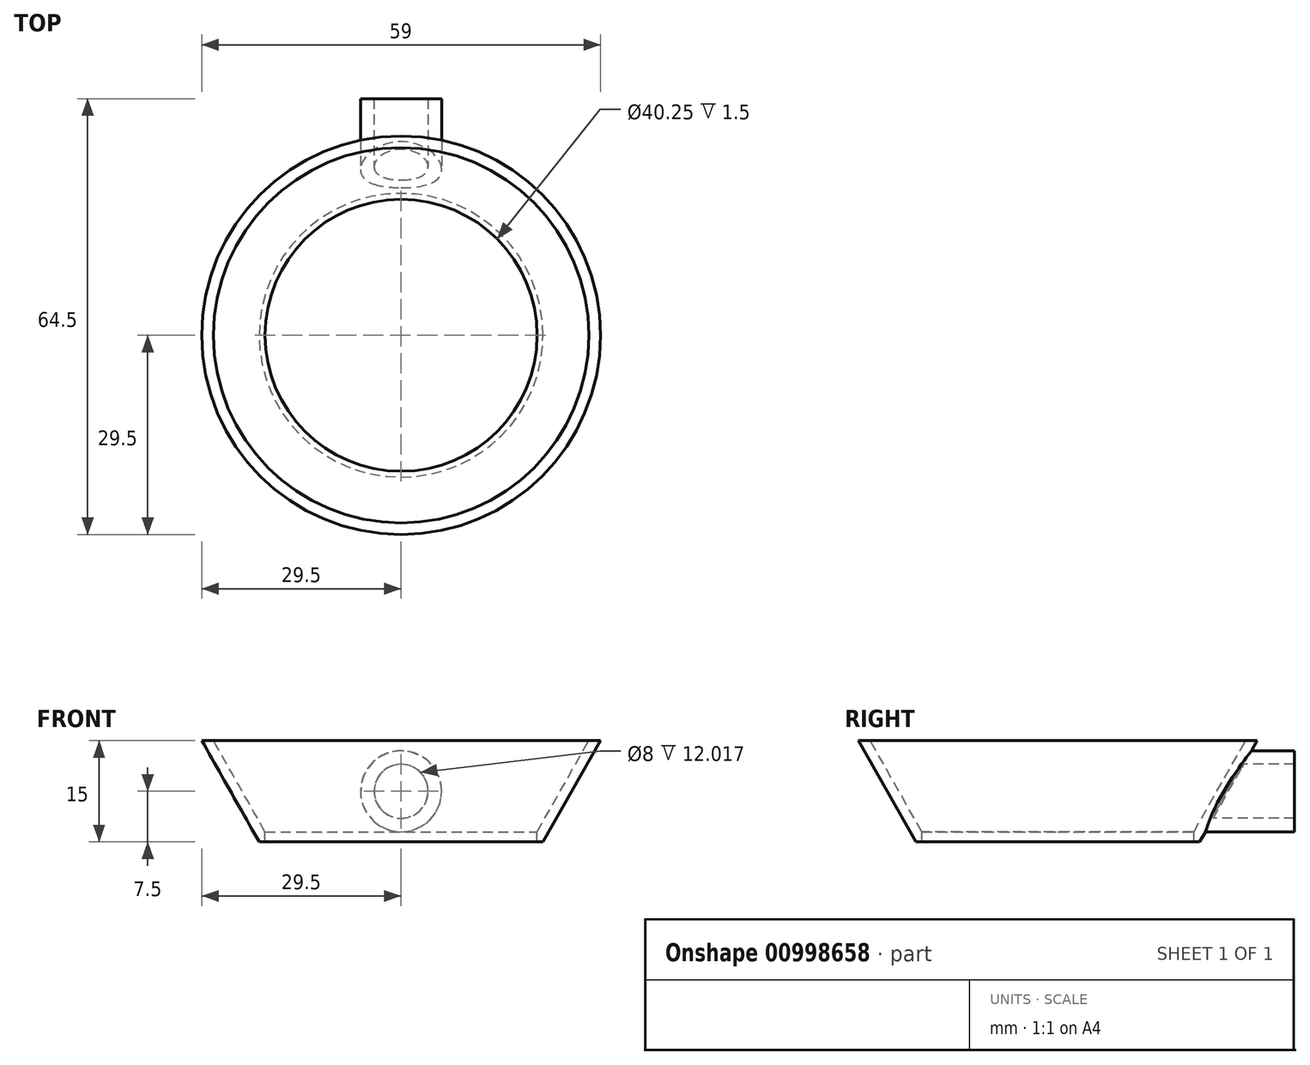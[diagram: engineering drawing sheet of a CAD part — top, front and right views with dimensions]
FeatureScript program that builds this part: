
annotation { "Feature Type Name" : "Feature", "Feature Type Description" : "" }
export const myFeature = defineFeature(function(context is Context, id is Id, definition is map)
    precondition{}
    {
        {
            var Q0;
            Q0=qCreatedBy(makeId("Right.planeOp"),FACE);
            var sketch = newSketch(context, id + "F0", { "sketchPlane" : qUnion([Q0])});
            skLineSegment(sketch, "E0", {"start": v(0, 0) * mm, "end": v(0, 60) * mm, "construction": true});
            skLineSegment(sketch, "E1", {"start": v(0, 60) * mm, "end": v(-46.5, 60) * mm, "construction": true});
            skLineSegment(sketch, "E2", {"start": v(-46.5, 60) * mm, "end": v(-12.5, 0) * mm, "construction": true});
            skLineSegment(sketch, "E3", {"start": v(-12.5, 0) * mm, "end": v(0, 0) * mm, "construction": true});
            skLineSegment(sketch, "E4", {"start": v(0, 15) * mm, "end": v(-21, 15) * mm});
            skLineSegment(sketch, "E5", {"start": v(0, 30) * mm, "end": v(-29.5, 30) * mm});
            skLineSegment(sketch, "E6", {"start": v(-29.5, 30) * mm, "end": v(-21, 15) * mm});
            skLineSegment(sketch, "E7", {"start": v(0, 30) * mm, "end": v(0, 15) * mm});
            skSolve(sketch);
        }
        {
            var Q0;
            Q0=qSketchRegion(id+"F0",true);
            var Q1;
            Q1=sQuery(id+"F0.wireOp",EDGE,"E0");
            revolve(context, id + "F1", {"surfaceOperationType" : NewSurfaceOperationType.NEW, "entities" : qUnion([Q0]), "axis" : qUnion([Q1]), "revolveType" : RevolveType.FULL});
        }
        {
            var Q0;
            Q0=qCreatedBy(makeId("Front.planeOp"),FACE);
            var sketch = newSketch(context, id + "F2", { "sketchPlane" : qUnion([Q0])});
            skCircle(sketch, "E8", {"center": v(0, 22.5) * mm, "radius": 4 * mm});
            skCircle(sketch, "E9", {"center": v(0, 22.5) * mm, "radius": 6 * mm});
            skSolve(sketch);
        }
        {
            var Q0;
            Q0=qSketchRegion(id+"F2",true);
            extrude(context, id + "F3", {"entities" : qUnion([Q0]), "operationType" : NewBodyOperationType.ADD, "oppositeDirection" : true, "depth" : 35 * mm, "offsetDistance" : 25 * mm});
        }
        {
            var Q0;
            Q0=makeQuery(id+"F1.opRevolve","SWEPT_FACE",FACE,{"disambiguationData":[OSD([sQuery(id+"F0.wireOp",EDGE,"E5")])]});
            shell(context, id + "F4", {"entities" : qUnion([Q0]), "thickness" : 1.5 * mm});
        }
        {
            var Q0;
            Q0=makeQuery(id+"F4.opShell","OFFSET_FACE",FACE,{"disambiguationData":[OSD([sQuery(id+"F0.wireOp",EDGE,"E4")])]});
            var sketch = newSketch(context, id + "F5", { "sketchPlane" : qUnion([Q0])});
            skCircle(sketch, "E10", {"center": v(0, 0) * mm, "radius": 20.13 * mm});
            skSolve(sketch);
        }
        {
            var Q0;
            Q0=qSketchRegion(id+"F5",true);
            extrude(context, id + "F6", {"entities" : qUnion([Q0]), "operationType" : NewBodyOperationType.REMOVE, "oppositeDirection" : true, "depth" : 25 * mm, "offsetDistance" : 25 * mm});
        }
    });
